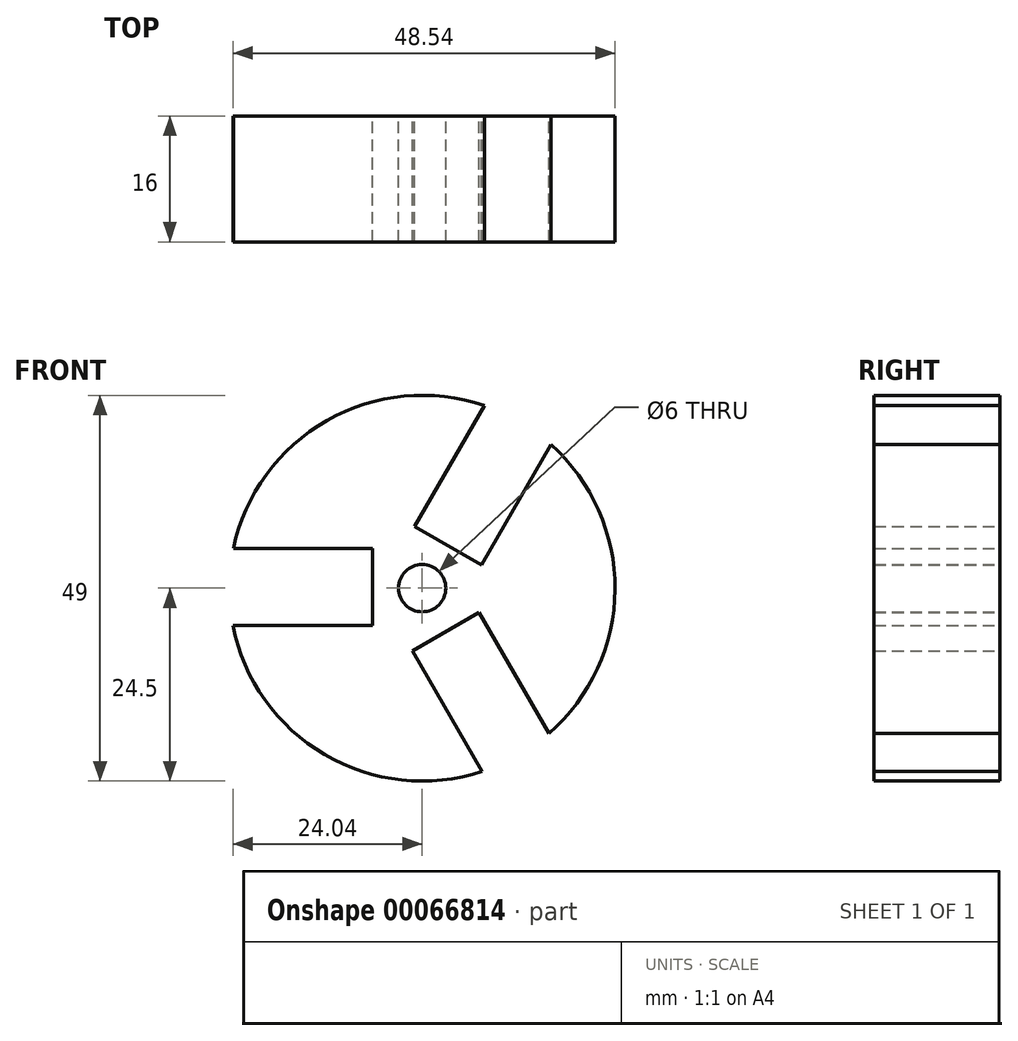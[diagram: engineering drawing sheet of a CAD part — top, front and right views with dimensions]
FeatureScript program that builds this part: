
annotation { "Feature Type Name" : "Feature", "Feature Type Description" : "" }
export const myFeature = defineFeature(function(context is Context, id is Id, definition is map)
    precondition{}
    {
        {
            var Q0;
            Q0=qCreatedBy(makeId("Front.planeOp"),FACE);
            var sketch = newSketch(context, id + "F0", { "sketchPlane" : qUnion([Q0])});
            skCircle(sketch, "E0", {"center": v(0, 0) * mm, "radius": 24.5 * mm});
            skCircle(sketch, "E1", {"center": v(0, 0) * mm, "radius": 3 * mm});
            skSolve(sketch);
        }
        {
            var Q0;
            Q0=makeQuery(id+"F0.imprint","IMPRINT",FACE,{"disambiguationData":[TD([[makeQuery(id+"F0.imprint","IMPRINT",EDGE,{"derivedFrom":sQuery(id+"F0.wireOp",EDGE,"E0")}),1.0]])]});
            extrude(context, id + "F1", {"entities" : qUnion([Q0]), "depth" : 16 * mm});
        }
        {
            var Q0;
            Q0=qCreatedBy(makeId("Front.planeOp"),FACE);
            var sketch = newSketch(context, id + "F2", { "sketchPlane" : qUnion([Q0])});
            skLineSegment(sketch, "E2.bottom", {"start": v(-32.76, 5.04) * mm, "end": v(-6.3, 5.04) * mm});
            skLineSegment(sketch, "E2.top", {"start": v(-32.76, -4.73) * mm, "end": v(-6.3, -4.73) * mm});
            skLineSegment(sketch, "E2.left", {"start": v(-32.76, 5.04) * mm, "end": v(-32.76, -4.73) * mm});
            skLineSegment(sketch, "E2.right", {"start": v(-6.3, 5.04) * mm, "end": v(-6.3, -4.73) * mm});
            skLineSegment(sketch, "E3.1.0", {"start": v(12.02, -30.9) * mm, "end": v(-1.21, -7.98) * mm});
            skLineSegment(sketch, "E3.1.1", {"start": v(20.47, -26) * mm, "end": v(7.24, -3.1) * mm});
            skLineSegment(sketch, "E3.1.2", {"start": v(12.02, -30.9) * mm, "end": v(20.47, -26) * mm});
            skLineSegment(sketch, "E3.1.3", {"start": v(-1.21, -7.98) * mm, "end": v(7.24, -3.1) * mm});
            skLineSegment(sketch, "E3.2.0", {"start": v(20.74, 25.85) * mm, "end": v(7.51, 2.94) * mm});
            skLineSegment(sketch, "E3.2.1", {"start": v(12.29, 30.73) * mm, "end": v(-0.94, 7.82) * mm});
            skLineSegment(sketch, "E3.2.2", {"start": v(20.74, 25.85) * mm, "end": v(12.29, 30.73) * mm});
            skLineSegment(sketch, "E3.2.3", {"start": v(7.51, 2.94) * mm, "end": v(-0.94, 7.82) * mm});
            skPoint(sketch, "E3.center", {"position": v(0, 0) * mm});
            skSolve(sketch);
        }
        {
            var Q0;
            Q0=makeQuery(id+"F2.imprint","IMPRINT",FACE,{"disambiguationData":[TD([[makeQuery(id+"F2.imprint","IMPRINT",EDGE,{"derivedFrom":sQuery(id+"F2.wireOp",EDGE,"E3.2.0")}),-1.0]])]});
            var Q1;
            Q1=makeQuery(id+"F2.imprint","IMPRINT",FACE,{"disambiguationData":[TD([[makeQuery(id+"F2.imprint","IMPRINT",EDGE,{"derivedFrom":sQuery(id+"F2.wireOp",EDGE,"E3.1.0")}),-1.0]])]});
            var Q2;
            Q2=makeQuery(id+"F2.imprint","IMPRINT",FACE,{"disambiguationData":[TD([[makeQuery(id+"F2.imprint","IMPRINT",EDGE,{"derivedFrom":sQuery(id+"F2.wireOp",EDGE,"E2.bottom")}),-1.0]])]});
            extrude(context, id + "F3", {"entities" : qUnion([Q0, Q1, Q2]), "operationType" : NewBodyOperationType.REMOVE, "depth" : 25 * mm});
        }
    });
